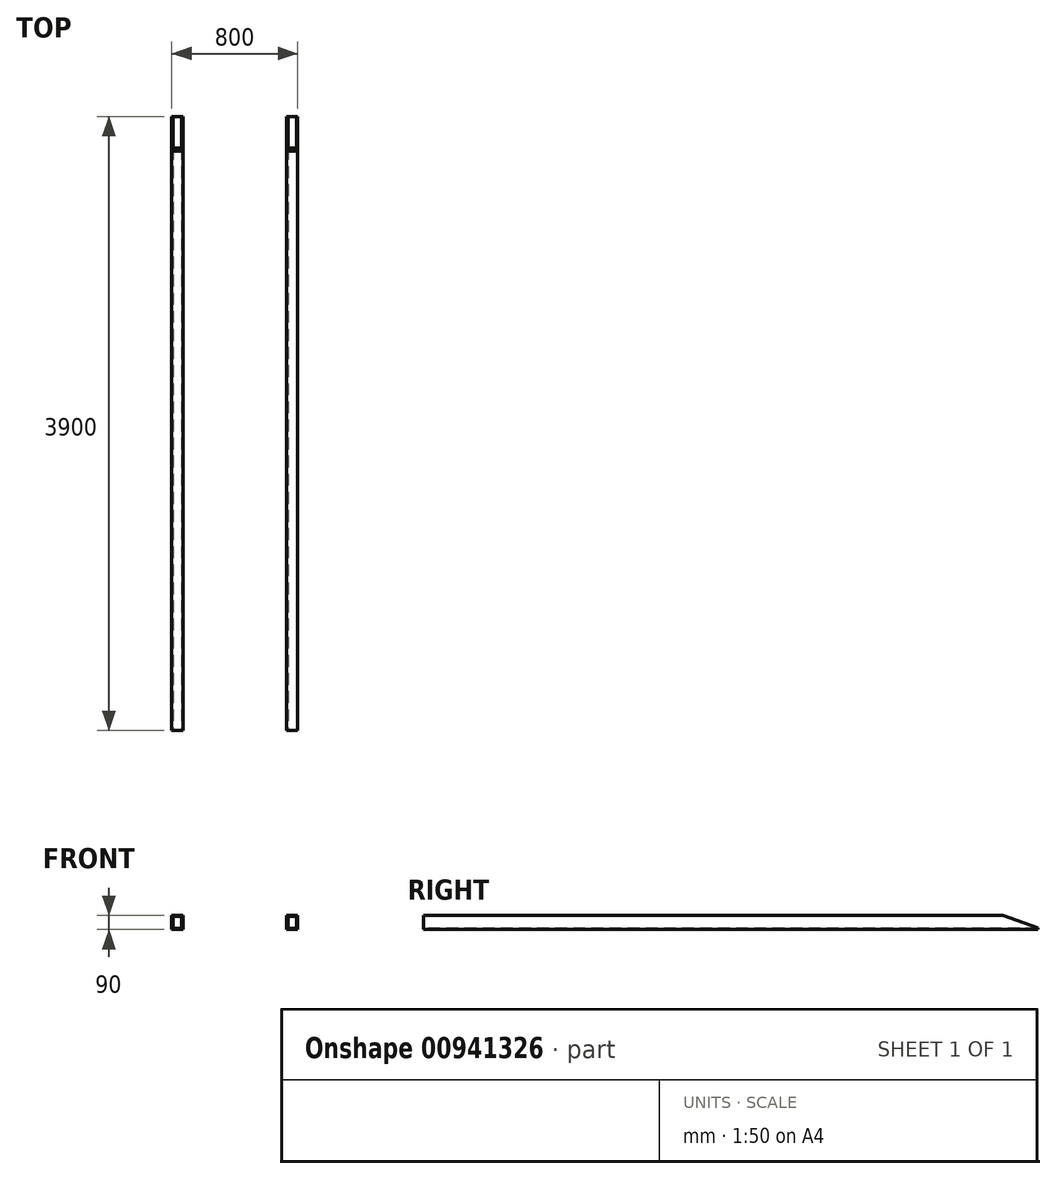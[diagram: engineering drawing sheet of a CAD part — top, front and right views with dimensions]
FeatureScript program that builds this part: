
annotation { "Feature Type Name" : "Feature", "Feature Type Description" : "" }
export const myFeature = defineFeature(function(context is Context, id is Id, definition is map)
    precondition{}
    {
        {
            var Q0;
            Q0=qCreatedBy(makeId("Front.planeOp"),FACE);
            var sketch = newSketch(context, id + "F0", { "sketchPlane" : qUnion([Q0])});
            skLineSegment(sketch, "E0.bottom", {"start": v(-34, 56.75) * mm, "end": v(22, 56.75) * mm});
            skLineSegment(sketch, "E0.top", {"start": v(-34, -19.25) * mm, "end": v(22, -19.25) * mm});
            skLineSegment(sketch, "E0.left", {"start": v(-34, 56.75) * mm, "end": v(-34, -19.25) * mm});
            skLineSegment(sketch, "E0.right", {"start": v(22, 56.75) * mm, "end": v(22, -19.25) * mm});
            skLineSegment(sketch, "E1.bottom", {"start": v(-41, 63.75) * mm, "end": v(29, 63.75) * mm});
            skLineSegment(sketch, "E1.top", {"start": v(-41, -26.25) * mm, "end": v(29, -26.25) * mm});
            skLineSegment(sketch, "E1.left", {"start": v(-41, 63.75) * mm, "end": v(-41, -26.25) * mm});
            skLineSegment(sketch, "E1.right", {"start": v(29, 63.75) * mm, "end": v(29, -26.25) * mm});
            skLineSegment(sketch, "E2.bottom", {"start": v(696, 56.75) * mm, "end": v(752, 56.75) * mm});
            skLineSegment(sketch, "E2.top", {"start": v(696, -19.25) * mm, "end": v(752, -19.25) * mm});
            skLineSegment(sketch, "E2.left", {"start": v(696, 56.75) * mm, "end": v(696, -19.25) * mm});
            skLineSegment(sketch, "E2.right", {"start": v(752, 56.75) * mm, "end": v(752, -19.25) * mm});
            skLineSegment(sketch, "E3.bottom", {"start": v(689, 63.75) * mm, "end": v(759, 63.75) * mm});
            skLineSegment(sketch, "E3.top", {"start": v(689, -26.25) * mm, "end": v(759, -26.25) * mm});
            skLineSegment(sketch, "E3.left", {"start": v(689, 63.75) * mm, "end": v(689, -26.25) * mm});
            skLineSegment(sketch, "E3.right", {"start": v(759, 63.75) * mm, "end": v(759, -26.25) * mm});
            skSolve(sketch);
        }
        {
            var Q0;
            Q0 = qSketchRegion(id + "F0", true);
            extrude(context, id + "F1", {"entities" : qUnion([Q0]), "oppositeDirection" : true, "depth" : 3900 * mm, "offsetDistance" : 25 * mm});
        }
        {
            var Q0;
            Q0=makeQuery(id+"F1.opExtrude","SWEPT_FACE",FACE,{"disambiguationData":[OSD([sQuery(id+"F0.wireOp",EDGE,"E3.right")])]});
            var sketch = newSketch(context, id + "F2", { "sketchPlane" : qUnion([Q0])});
            skLineSegment(sketch, "E4", {"start": v(3680, 63.75) * mm, "end": v(3900, -16.25) * mm});
            skLineSegment(sketch, "E5", {"start": v(3900, -16.25) * mm, "end": v(3900, 63.75) * mm});
            skLineSegment(sketch, "E6", {"start": v(3900, 63.75) * mm, "end": v(3680, 63.75) * mm});
            skSolve(sketch);
        }
        {
            var Q0;
            Q0 = qSketchRegion(id + "F2", true);
            extrude(context, id + "F3", {"entities" : qUnion([Q0]), "operationType" : NewBodyOperationType.REMOVE, "endBound" : BoundingType.THROUGH_ALL, "oppositeDirection" : true, "depth" : 25 * mm, "offsetDistance" : 25 * mm});
        }
        {
            var Q0;
            Q0=makeQuery(id+"F1.opExtrude","SWEPT_FACE",FACE,{"disambiguationData":[OSD([sQuery(id+"F0.wireOp",EDGE,"E1.right")])]});
            var sketch = newSketch(context, id + "F4", { "sketchPlane" : qUnion([Q0])});
            skLineSegment(sketch, "E7", {"start": v(3680, 63.75) * mm, "end": v(3900, -16.25) * mm});
            skLineSegment(sketch, "E8", {"start": v(3900, -16.25) * mm, "end": v(3900, 63.75) * mm});
            skLineSegment(sketch, "E9", {"start": v(3900, 63.75) * mm, "end": v(3680, 63.75) * mm});
            skSolve(sketch);
        }
        {
            var Q0;
            Q0 = qSketchRegion(id + "F4", true);
            extrude(context, id + "F5", {"entities" : qUnion([Q0]), "operationType" : NewBodyOperationType.REMOVE, "endBound" : BoundingType.THROUGH_ALL, "oppositeDirection" : true, "depth" : 25 * mm, "offsetDistance" : 25 * mm});
        }
    });
